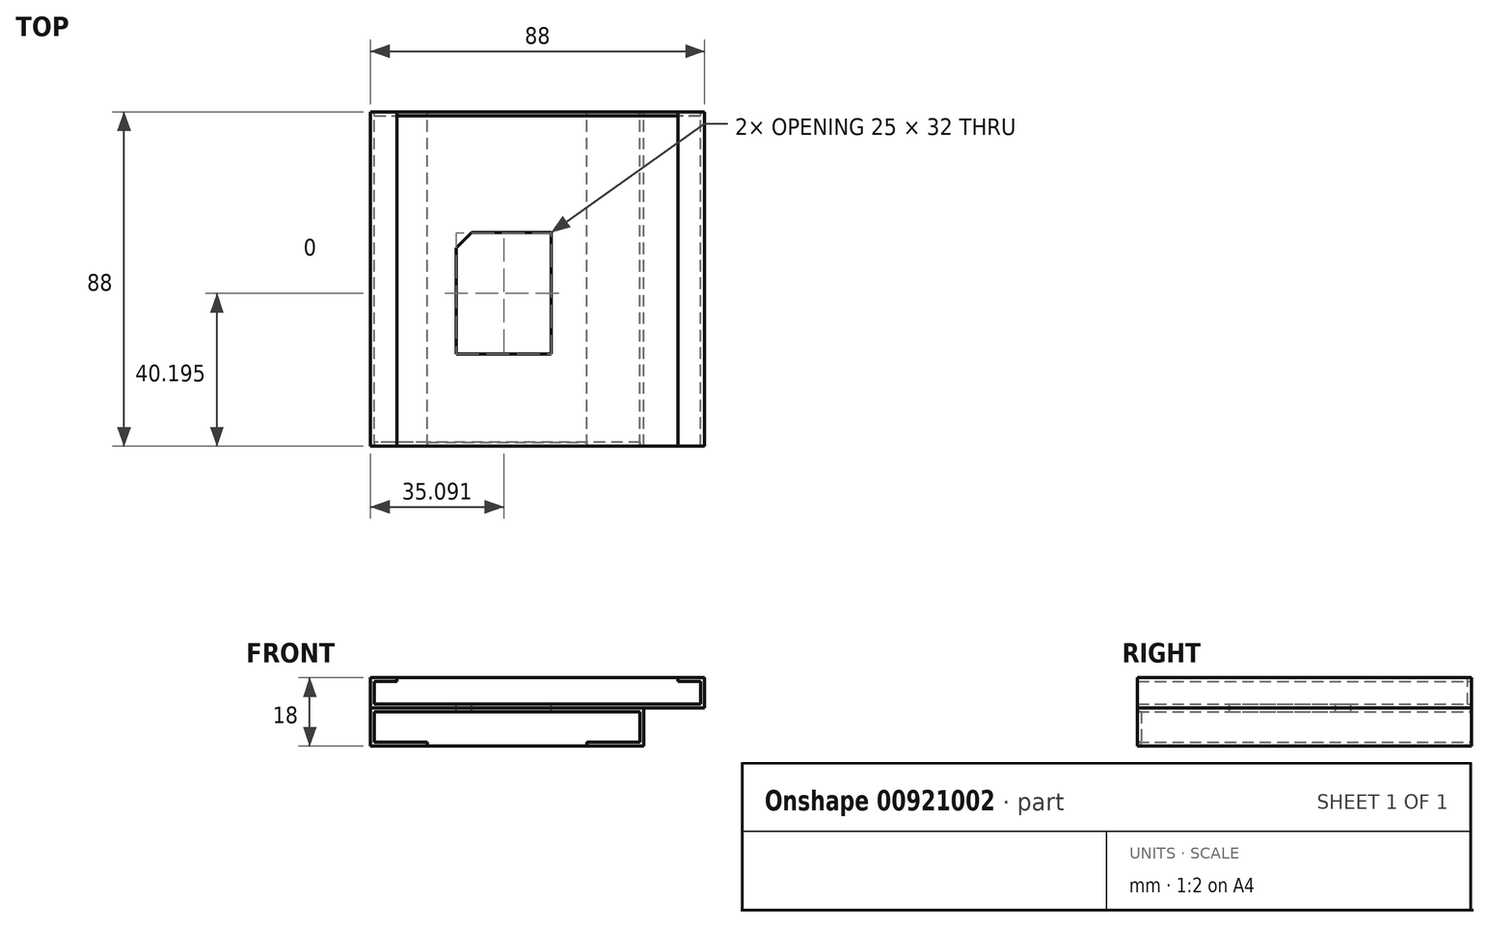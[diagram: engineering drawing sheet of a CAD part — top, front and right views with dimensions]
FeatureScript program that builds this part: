
annotation { "Feature Type Name" : "Feature", "Feature Type Description" : "" }
export const myFeature = defineFeature(function(context is Context, id is Id, definition is map)
    precondition{}
    {
        {
            var Q0;
            Q0=qCreatedBy(makeId("Front.planeOp"),FACE);
            var sketch = newSketch(context, id + "F0", { "sketchPlane" : qUnion([Q0])});
            skLineSegment(sketch, "E0", {"start": v(0, 0) * mm, "end": v(-43, 0) * mm});
            skLineSegment(sketch, "E1", {"start": v(-43, 0) * mm, "end": v(-43, 6) * mm});
            skLineSegment(sketch, "E2", {"start": v(-43, 6) * mm, "end": v(-37, 6) * mm});
            skLineSegment(sketch, "E3.MirrorCS", {"start": v(43, 6) * mm, "end": v(37, 6) * mm});
            skLineSegment(sketch, "E4.MirrorCS", {"start": v(43, 0) * mm, "end": v(43, 6) * mm});
            skLineSegment(sketch, "E5.MirrorCS", {"start": v(0, 0) * mm, "end": v(43, 0) * mm});
            skLineSegment(sketch, "E6", {"start": v(37, 6) * mm, "end": v(37, 7) * mm});
            skLineSegment(sketch, "E7", {"start": v(37, 7) * mm, "end": v(44, 7) * mm});
            skLineSegment(sketch, "E8", {"start": v(44, 7) * mm, "end": v(44, -1) * mm});
            skLineSegment(sketch, "E9", {"start": v(44, -1) * mm, "end": v(0, -1) * mm});
            skLineSegment(sketch, "E10.MirrorCS", {"start": v(-37, 7) * mm, "end": v(-44, 7) * mm});
            skLineSegment(sketch, "E11.MirrorCS", {"start": v(-37, 6) * mm, "end": v(-37, 7) * mm});
            skLineSegment(sketch, "E12.MirrorCS", {"start": v(-44, 7) * mm, "end": v(-44, -1) * mm});
            skLineSegment(sketch, "E13.MirrorCS", {"start": v(-44, -1) * mm, "end": v(0, -1) * mm});
            skLineSegment(sketch, "E14.MirrorCS", {"start": v(0, -2) * mm, "end": v(27, -2) * mm});
            skLineSegment(sketch, "E15.MirrorCS", {"start": v(0, -2) * mm, "end": v(-43, -2) * mm});
            skLineSegment(sketch, "E16", {"start": v(-44, -1) * mm, "end": v(-44, -11) * mm});
            skLineSegment(sketch, "E17", {"start": v(-44, -11) * mm, "end": v(-29, -11) * mm});
            skLineSegment(sketch, "E18", {"start": v(-29, -11) * mm, "end": v(-29, -10) * mm});
            skLineSegment(sketch, "E19", {"start": v(-29, -10) * mm, "end": v(-43, -10) * mm});
            skLineSegment(sketch, "E20", {"start": v(-43, -10) * mm, "end": v(-43, -2) * mm});
            skPoint(sketch, "E21", {"position": v(27, -2) * mm});
            skPoint(sketch, "E22", {"position": v(28, -2) * mm});
            skLineSegment(sketch, "E23", {"start": v(27, -2) * mm, "end": v(27, -10) * mm});
            skLineSegment(sketch, "E24", {"start": v(27, -10) * mm, "end": v(13, -10) * mm});
            skLineSegment(sketch, "E25", {"start": v(13, -10) * mm, "end": v(13, -11) * mm});
            skLineSegment(sketch, "E26", {"start": v(13, -11) * mm, "end": v(28, -11) * mm});
            skLineSegment(sketch, "E27", {"start": v(28, -11) * mm, "end": v(28, -2) * mm});
            skLineSegment(sketch, "E28", {"start": v(28, -2) * mm, "end": v(28, -1) * mm});
            skSolve(sketch);
        }
        {
            var Q0;
            Q0=makeQuery(id+"F0.imprint","IMPRINT",FACE,{"disambiguationData":[TD([[makeQuery(id+"F0.imprint","IMPRINT",EDGE,{"derivedFrom":sQuery(id+"F0.wireOp",EDGE,"E0")}),1.0]])]});
            extrude(context, id + "F1", {"entities" : qUnion([Q0]), "depth" : 88 * mm, "offsetDistance" : 25 * mm});
        }
        {
            var Q0;
            Q0=makeQuery(id+"F1.opExtrude","CAP_FACE",FACE,{"disambiguationData":[OSD([sQuery(id+"F0.wireOp",EDGE,"E0"),sQuery(id+"F0.wireOp",EDGE,"E1"),sQuery(id+"F0.wireOp",EDGE,"E2"),sQuery(id+"F0.wireOp",EDGE,"E3.MirrorCS"),sQuery(id+"F0.wireOp",EDGE,"E4.MirrorCS"),sQuery(id+"F0.wireOp",EDGE,"E5.MirrorCS"),sQuery(id+"F0.wireOp",EDGE,"E6"),sQuery(id+"F0.wireOp",EDGE,"E7"),sQuery(id+"F0.wireOp",EDGE,"E8"),sQuery(id+"F0.wireOp",EDGE,"E9"),sQuery(id+"F0.wireOp",EDGE,"E10.MirrorCS"),sQuery(id+"F0.wireOp",EDGE,"E11.MirrorCS"),sQuery(id+"F0.wireOp",EDGE,"E12.MirrorCS"),sQuery(id+"F0.wireOp",EDGE,"E13.MirrorCS")])],"isStart":true});
            var sketch = newSketch(context, id + "F2", { "sketchPlane" : qUnion([Q0])});
            skLineSegment(sketch, "E29.bottom", {"start": v(-44, 7) * mm, "end": v(44, 7) * mm});
            skLineSegment(sketch, "E29.top", {"start": v(-44, -1) * mm, "end": v(44, -1) * mm});
            skLineSegment(sketch, "E29.left", {"start": v(-44, 7) * mm, "end": v(-44, -1) * mm});
            skLineSegment(sketch, "E29.right", {"start": v(44, 7) * mm, "end": v(44, -1) * mm});
            skSolve(sketch);
        }
        {
            var Q0;
            Q0=makeQuery(id+"F2.imprint","IMPRINT",FACE,{"disambiguationData":[TD([[makeQuery(id+"F2.imprint","IMPRINT",EDGE,{"derivedFrom":makeQuery(id+"F1.opExtrude","CAP_EDGE",EDGE,{"disambiguationData":[OSD([sQuery(id+"F0.wireOp",EDGE,"E1")])],"isStart":true})}),1.0]])]});
            extrude(context, id + "F3", {"entities" : qUnion([Q0]), "oppositeDirection" : true, "depth" : 1 * mm, "offsetDistance" : 25 * mm});
        }
        {
            var Q0;
            {var subQ0=sQuery(id+"F0.wireOp",EDGE,"E13.MirrorCS");Q0=makeQuery(id+"F0.imprint","IMPRINT",FACE,{"disambiguationData":[TD([[makeQuery(id+"F0.imprint","IMPRINT",EDGE,{"derivedFrom":subQ0}),-1.0]])]});}
            extrude(context, id + "F4", {"entities" : qUnion([Q0]), "depth" : 88 * mm, "offsetDistance" : 25 * mm});
        }
        {
            var Q0;
            Q0=makeQuery(id+"F4.opExtrude","CAP_FACE",FACE,{"disambiguationData":[OSD([sQuery(id+"F0.wireOp",EDGE,"E9"),sQuery(id+"F0.wireOp",EDGE,"E13.MirrorCS"),sQuery(id+"F0.wireOp",EDGE,"E14.MirrorCS"),sQuery(id+"F0.wireOp",EDGE,"E15.MirrorCS"),sQuery(id+"F0.wireOp",EDGE,"E16"),sQuery(id+"F0.wireOp",EDGE,"E17"),sQuery(id+"F0.wireOp",EDGE,"E18"),sQuery(id+"F0.wireOp",EDGE,"E19"),sQuery(id+"F0.wireOp",EDGE,"E20"),sQuery(id+"F0.wireOp",EDGE,"E23"),sQuery(id+"F0.wireOp",EDGE,"E24"),sQuery(id+"F0.wireOp",EDGE,"E25"),sQuery(id+"F0.wireOp",EDGE,"E26"),sQuery(id+"F0.wireOp",EDGE,"E27"),sQuery(id+"F0.wireOp",EDGE,"E28")])],"isStart":false});
            var sketch = newSketch(context, id + "F5", { "sketchPlane" : qUnion([Q0])});
            skLineSegment(sketch, "E30.bottom", {"start": v(-44, -1) * mm, "end": v(28, -1) * mm});
            skLineSegment(sketch, "E30.top", {"start": v(-44, -11) * mm, "end": v(28, -11) * mm});
            skLineSegment(sketch, "E30.left", {"start": v(-44, -1) * mm, "end": v(-44, -11) * mm});
            skLineSegment(sketch, "E30.right", {"start": v(28, -1) * mm, "end": v(28, -11) * mm});
            skSolve(sketch);
        }
        {
            var Q0;
            {var subQ0=makeQuery(id+"F4.opExtrude","CAP_EDGE",EDGE,{"disambiguationData":[OSD([sQuery(id+"F0.wireOp",EDGE,"E18")])],"isStart":false});Q0=makeQuery(id+"F5.imprint","IMPRINT",FACE,{"disambiguationData":[TD([[makeQuery(id+"F5.imprint","IMPRINT",EDGE,{"derivedFrom":subQ0}),-1.0]])]});}
            extrude(context, id + "F6", {"entities" : qUnion([Q0]), "oppositeDirection" : true, "depth" : 1 * mm, "offsetDistance" : 25 * mm});
        }
        {
            var Q0;
            Q0=qCreatedBy(makeId("Top.planeOp"),FACE);
            var sketch = newSketch(context, id + "F7", { "sketchPlane" : qUnion([Q0])});
            skLineSegment(sketch, "E31.MirrorCS", {"start": v(3.6, -63.8) * mm, "end": v(-21.4, -63.8) * mm});
            skLineSegment(sketch, "E32.MirrorCS", {"start": v(3.6, -63.8) * mm, "end": v(3.6, -31.8) * mm});
            skLineSegment(sketch, "E33.MirrorCS", {"start": v(-21.4, -63.8) * mm, "end": v(-21.4, -35.8) * mm});
            skLineSegment(sketch, "E34.MirrorCS", {"start": v(-21.4, -35.8) * mm, "end": v(-17.4, -31.8) * mm});
            skLineSegment(sketch, "E35.MirrorCS", {"start": v(3.6, -31.8) * mm, "end": v(-17.4, -31.8) * mm});
            skSolve(sketch);
        }
        {
            var Q0;
            Q0 = qSketchRegion(id + "F7", true);
            extrude(context, id + "F8", {"entities" : qUnion([Q0]), "operationType" : NewBodyOperationType.REMOVE, "oppositeDirection" : true, "depth" : 2 * mm, "offsetDistance" : 25 * mm});
        }
    });
